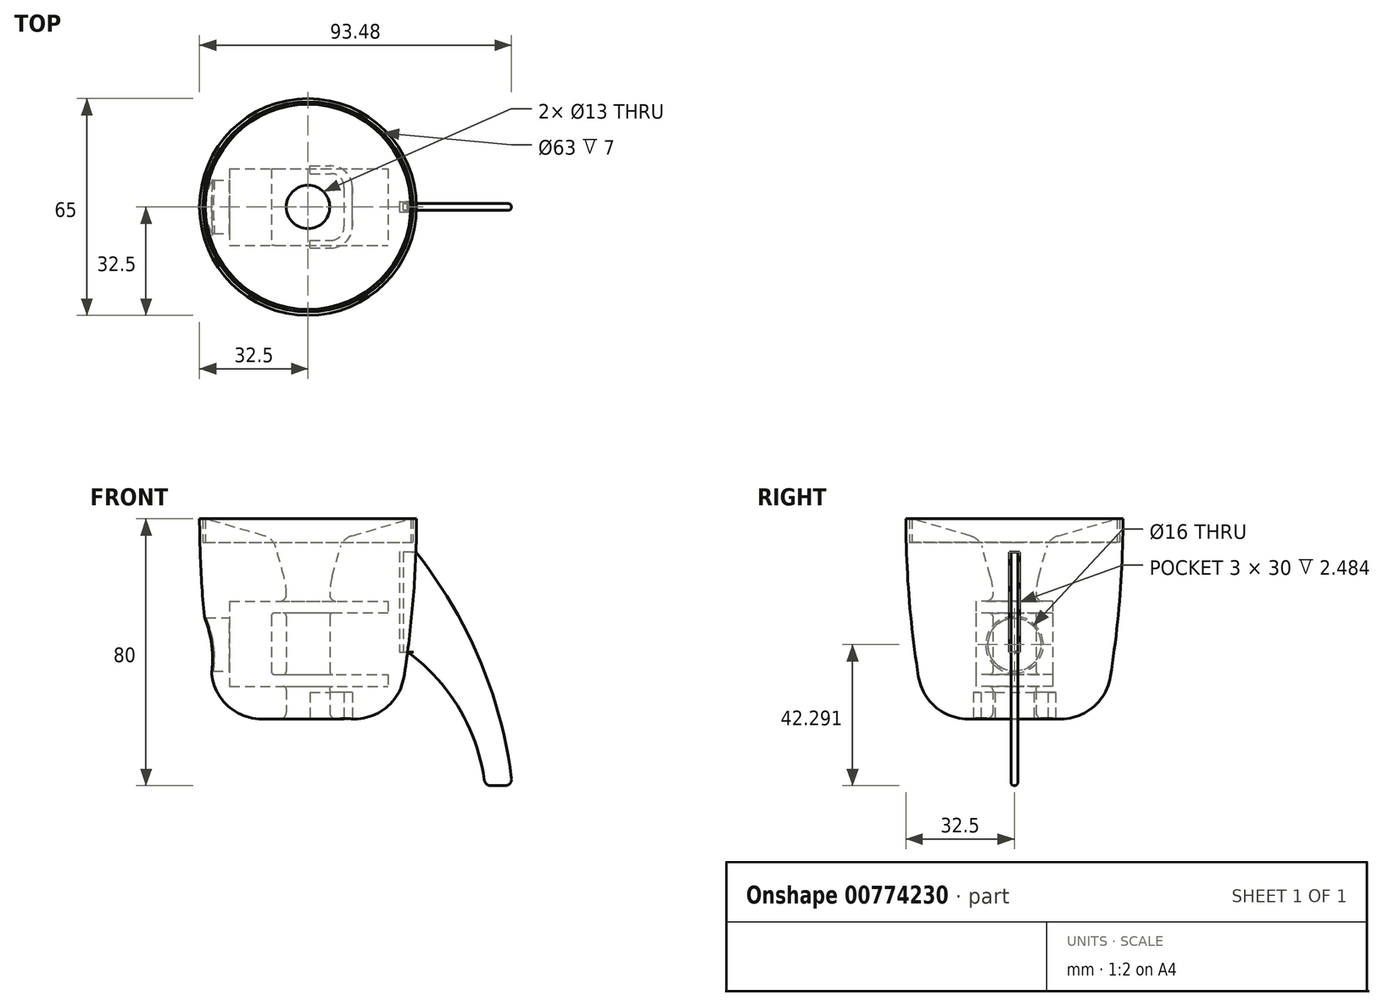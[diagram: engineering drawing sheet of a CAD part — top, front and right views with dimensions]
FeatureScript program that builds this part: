
annotation { "Feature Type Name" : "Feature", "Feature Type Description" : "" }
export const myFeature = defineFeature(function(context is Context, id is Id, definition is map)
    precondition{}
    {
        {
            var Q0;
            Q0=qCreatedBy(makeId("Front.planeOp"),FACE);
            var sketch = newSketch(context, id + "F0", { "sketchPlane" : qUnion([Q0])});
            skLineSegment(sketch, "E0", {"start": v(-32.5, -33.38) * mm, "end": v(-32.5, 26.62) * mm, "construction": true});
            skLineSegment(sketch, "E1", {"start": v(-30.75, 26.62) * mm, "end": v(-13.09, 21.53) * mm});
            skLineSegment(sketch, "E2", {"start": v(-9.65, 18.05) * mm, "end": v(-7.22, 9.22) * mm});
            skLineSegment(sketch, "E3", {"start": v(-6.5, 3.91) * mm, "end": v(-6.5, -33.38) * mm});
            skLineSegment(sketch, "E4", {"start": v(-6.5, -33.38) * mm, "end": v(-32.5, -33.38) * mm, "construction": true});
            skLineSegment(sketch, "E5", {"start": v(0, -36.56) * mm, "end": v(0, 42.73) * mm, "construction": true});
            skArc(sketch, "E6", {"start": v(-32.5, 26.62) * mm, "mid": v(-31.56, 2.88) * mm, "end": v(-28.74, -20.7) * mm});
            skLineSegment(sketch, "E7.bottom", {"start": v(-25.31, 12.07) * mm, "end": v(8.69, 12.07) * mm, "construction": true});
            skLineSegment(sketch, "E7.top", {"start": v(-25.31, -7.93) * mm, "end": v(8.69, -7.93) * mm, "construction": true});
            skLineSegment(sketch, "E7.left", {"start": v(-25.31, 12.07) * mm, "end": v(-25.31, -7.93) * mm, "construction": true});
            skLineSegment(sketch, "E7.right", {"start": v(8.69, 12.07) * mm, "end": v(8.69, -7.93) * mm, "construction": true});
            skLineSegment(sketch, "E8", {"start": v(-32.5, 26.62) * mm, "end": v(-31.5, 26.62) * mm});
            skLineSegment(sketch, "E9", {"start": v(-31.5, 26.62) * mm, "end": v(-31.5, 19.62) * mm});
            skLineSegment(sketch, "E10", {"start": v(-31.5, 19.62) * mm, "end": v(-30.75, 19.62) * mm});
            skLineSegment(sketch, "E11", {"start": v(-30.75, 19.62) * mm, "end": v(-30.75, 26.62) * mm});
            skLineSegment(sketch, "E12", {"start": v(-6.5, -33.38) * mm, "end": v(-6.5, -33.38) * mm});
            skLineSegment(sketch, "E13", {"start": v(-6.5, -33.38) * mm, "end": v(-13.88, -33.38) * mm});
            skPoint(sketch, "E14.visualSharp", {"position": v(-10.4, 20.75) * mm});
            skArc(sketch, "E14.filletArc", {"start": v(-9.65, 18.05) * mm, "mid": v(-10.92, 20.24) * mm, "end": v(-13.09, 21.53) * mm});
            skPoint(sketch, "E15.visualSharp", {"position": v(-6.5, 6.62) * mm});
            skArc(sketch, "E15.filletArc", {"start": v(-6.5, 3.91) * mm, "mid": v(-6.68, 6.6) * mm, "end": v(-7.22, 9.22) * mm});
            skArc(sketch, "E16", {"start": v(-28.74, -20.7) * mm, "mid": v(-23.65, -29.78) * mm, "end": v(-13.88, -33.38) * mm});
            skSolve(sketch);
        }
        {
            var Q0;
            Q0 = qSketchRegion(id + "F0", true);
            var Q1;
            Q1=sQuery(id+"F0.wireOp",EDGE,"E5");
            revolve(context, id + "F1", {"surfaceOperationType" : NewSurfaceOperationType.NEW, "entities" : qUnion([Q0]), "axis" : qUnion([Q1]), "revolveType" : RevolveType.FULL});
        }
        {
            var Q0;
            Q0=qCreatedBy(makeId("Front.planeOp"),FACE);
            var sketch = newSketch(context, id + "F2", { "sketchPlane" : qUnion([Q0])});
            skLineSegment(sketch, "E17.bottom", {"start": v(-23.5, 1.91) * mm, "end": v(24, 1.91) * mm});
            skLineSegment(sketch, "E17.top", {"start": v(-23.5, -23.59) * mm, "end": v(24, -23.59) * mm});
            skLineSegment(sketch, "E17.left", {"start": v(-23.5, 1.91) * mm, "end": v(-23.5, -23.59) * mm});
            skLineSegment(sketch, "E17.right", {"start": v(24, 1.91) * mm, "end": v(24, -23.59) * mm, "construction": true});
            skLineSegment(sketch, "E18", {"start": v(24, 1.91) * mm, "end": v(24, -1.59) * mm});
            skLineSegment(sketch, "E19", {"start": v(24, -1.59) * mm, "end": v(-11, -1.59) * mm});
            skLineSegment(sketch, "E20", {"start": v(-11, -1.59) * mm, "end": v(-11, -20.09) * mm});
            skLineSegment(sketch, "E21", {"start": v(-11, -20.09) * mm, "end": v(24, -20.09) * mm});
            skLineSegment(sketch, "E22", {"start": v(24, -20.09) * mm, "end": v(24, -23.59) * mm});
            skSolve(sketch);
        }
        {
            var Q0;
            Q0 = qSketchRegion(id + "F2", true);
            extrude(context, id + "F3", {"entities" : qUnion([Q0]), "operationType" : NewBodyOperationType.REMOVE, "oppositeDirection" : true, "depth" : 23 * mm, "offsetDistance" : 25 * mm, "symmetric" : true});
        }
        {
            var Q0;
            Q0=qCreatedBy(makeId("Right.planeOp"),FACE);
            cPlane(context, id + "F4", {"entities" : qUnion([Q0]), "cplaneType" : CPlaneType.OFFSET, "offset" : 18 * mm, "oppositeDirection" : true, "width" : 150 * mm, "height" : 150 * mm});
        }
        {
            var Q0;
            Q0=qCreatedBy(id+"F4.planeOp",FACE);
            var sketch = newSketch(context, id + "F5", { "sketchPlane" : qUnion([Q0])});
            skCircle(sketch, "E23", {"center": v(0, -11.09) * mm, "radius": 8 * mm});
            skSolve(sketch);
        }
        {
            var Q0;
            Q0 = qSketchRegion(id + "F5", true);
            extrude(context, id + "F6", {"entities" : qUnion([Q0]), "operationType" : NewBodyOperationType.REMOVE, "oppositeDirection" : true, "depth" : 25 * mm, "offsetDistance" : 25 * mm});
        }
        {
            var Q0;
            Q0=makeQuery(id+"F6.boolean.opBoolean","INTERSECT",EDGE,{"derivedFrom":[makeQuery(id+"F1.opRevolve","SWEPT_FACE",FACE,{"disambiguationData":[OSD([sQuery(id+"F0.wireOp",EDGE,"E6")])]}),makeQuery(id+"F6.opExtrude","SWEPT_FACE",FACE,{"disambiguationData":[OSD([sQuery(id+"F5.wireOp",EDGE,"E23")])]})]});
            fillet(context, id + "F7", {"entities" : qUnion([Q0]), "radius" : 0.5 * mm, "tangentPropagation" : true, "allowEdgeOverflow" : false});
        }
        {
            var Q0;
            Q0=makeQuery(id+"F1.opRevolve","SWEPT_EDGE",EDGE,{"disambiguationData":[OSD([sQuery(id+"F0.wireOp",EDGE,"E12"),sQuery(id+"F0.wireOp",EDGE,"E13")])]});
            fillet(context, id + "F8", {"entities" : qUnion([Q0]), "radius" : 2 * mm, "tangentPropagation" : true, "allowEdgeOverflow" : false});
        }
        {
            var Q0;
            Q0=makeQuery(id+"F3.boolean.opBoolean","INTERSECT",EDGE,{"derivedFrom":[makeQuery(id+"F1.opRevolve","SWEPT_FACE",FACE,{"disambiguationData":[OSD([sQuery(id+"F0.wireOp",EDGE,"E3"),sQuery(id+"F0.wireOp",EDGE,"E12")])]}),makeQuery(id+"F3.opExtrude","SWEPT_FACE",FACE,{"disambiguationData":[OSD([sQuery(id+"F2.wireOp",EDGE,"E17.top")])]})]});
            var Q1;
            Q1=makeQuery(id+"F3.boolean.opBoolean","INTERSECT",EDGE,{"derivedFrom":[makeQuery(id+"F1.opRevolve","SWEPT_FACE",FACE,{"disambiguationData":[OSD([sQuery(id+"F0.wireOp",EDGE,"E3"),sQuery(id+"F0.wireOp",EDGE,"E12")])]}),makeQuery(id+"F3.opExtrude","SWEPT_FACE",FACE,{"disambiguationData":[OSD([sQuery(id+"F2.wireOp",EDGE,"E21")])]})]});
            var Q2;
            Q2=makeQuery(id+"F3.boolean.opBoolean","INTERSECT",EDGE,{"derivedFrom":[makeQuery(id+"F1.opRevolve","SWEPT_FACE",FACE,{"disambiguationData":[OSD([sQuery(id+"F0.wireOp",EDGE,"E3"),sQuery(id+"F0.wireOp",EDGE,"E12")])]}),makeQuery(id+"F3.opExtrude","SWEPT_FACE",FACE,{"disambiguationData":[OSD([sQuery(id+"F2.wireOp",EDGE,"E19")])]})]});
            var Q3;
            Q3=makeQuery(id+"F3.boolean.opBoolean","COPY",EDGE,{"derivedFrom":makeQuery(id+"F3.opExtrude","SWEPT_EDGE",EDGE,{"disambiguationData":[OSD([sQuery(id+"F2.wireOp",EDGE,"E19"),sQuery(id+"F2.wireOp",EDGE,"E20")])]})});
            var Q4;
            Q4=makeQuery(id+"F3.boolean.opBoolean","COPY",EDGE,{"derivedFrom":makeQuery(id+"F3.opExtrude","SWEPT_EDGE",EDGE,{"disambiguationData":[OSD([sQuery(id+"F2.wireOp",EDGE,"E20"),sQuery(id+"F2.wireOp",EDGE,"E21")])]})});
            fillet(context, id + "F9", {"entities" : qUnion([Q0, Q1, Q2, Q3, Q4]), "radius" : 1 * mm, "tangentPropagation" : true, "allowEdgeOverflow" : false});
        }
        {
            var Q0;
            Q0=qCreatedBy(makeId("Front.planeOp"),FACE);
            var sketch = newSketch(context, id + "F10", { "sketchPlane" : qUnion([Q0])});
            skLineSegment(sketch, "E24", {"start": v(0.05, 26.62) * mm, "end": v(33.55, 26.62) * mm, "construction": true});
            skLineSegment(sketch, "E25", {"start": v(0.05, 26.62) * mm, "end": v(-32.5, 26.62) * mm, "construction": true});
            skArc(sketch, "E26", {"start": v(-32.5, 26.62) * mm, "mid": v(-31.56, 2.88) * mm, "end": v(-28.74, -20.7) * mm, "construction": true});
            skArc(sketch, "E27.MirrorCS", {"start": v(32.5, 26.62) * mm, "mid": v(31.56, 2.88) * mm, "end": v(28.74, -20.7) * mm, "construction": true});
            skArc(sketch, "E28", {"start": v(29.82, -13.38) * mm, "mid": v(31.45, 1.58) * mm, "end": v(32.33, 16.62) * mm});
            skLineSegment(sketch, "E29", {"start": v(32.33, 16.62) * mm, "end": v(27.33, 16.62) * mm});
            skLineSegment(sketch, "E30", {"start": v(27.33, 16.62) * mm, "end": v(27.33, -13.38) * mm});
            skLineSegment(sketch, "E31", {"start": v(27.33, -13.38) * mm, "end": v(29.82, -13.38) * mm});
            skLineSegment(sketch, "E32", {"start": v(0.05, 26.62) * mm, "end": v(0, 0) * mm, "construction": true});
            skSolve(sketch);
        }
        {
            var Q0;
            Q0 = qSketchRegion(id + "F10", true);
            extrude(context, id + "F11", {"entities" : qUnion([Q0]), "operationType" : NewBodyOperationType.REMOVE, "oppositeDirection" : true, "depth" : 3 * mm, "offsetDistance" : 25 * mm, "symmetric" : true});
        }
        {
            var Q0;
            Q0=qCreatedBy(makeId("Front.planeOp"),FACE);
            var sketch = newSketch(context, id + "F12", { "sketchPlane" : qUnion([Q0])});
            skLineSegment(sketch, "E33", {"start": v(32.32, 16.62) * mm, "end": v(28.5, 16.62) * mm});
            skLineSegment(sketch, "E34", {"start": v(28.5, 16.62) * mm, "end": v(28.5, -13.38) * mm});
            skLineSegment(sketch, "E35", {"start": v(28.5, -13.38) * mm, "end": v(29.94, -13.38) * mm});
            skLineSegment(sketch, "E36", {"start": v(54.8, -53.38) * mm, "end": v(58.98, -53.38) * mm});
            skArc(sketch, "E37", {"start": v(60.97, -51.13) * mm, "mid": v(51.29, -15.3) * mm, "end": v(32.32, 16.62) * mm});
            skArc(sketch, "E38", {"start": v(52.82, -51.66) * mm, "mid": v(45.26, -30.2) * mm, "end": v(29.94, -13.38) * mm});
            skPoint(sketch, "E39.visualSharp", {"position": v(53.03, -53.38) * mm});
            skArc(sketch, "E39.filletArc", {"start": v(52.82, -51.66) * mm, "mid": v(53.48, -52.9) * mm, "end": v(54.8, -53.38) * mm});
            skPoint(sketch, "E40.visualSharp", {"position": v(61.24, -53.38) * mm});
            skArc(sketch, "E40.filletArc", {"start": v(58.98, -53.38) * mm, "mid": v(60.48, -52.7) * mm, "end": v(60.97, -51.13) * mm});
            skSolve(sketch);
        }
        {
            var Q0;
            Q0 = qSketchRegion(id + "F12", true);
            extrude(context, id + "F13", {"entities" : qUnion([Q0]), "depth" : 2 * mm, "offsetDistance" : 25 * mm, "symmetric" : true});
        }
        {
            var Q0;
            Q0=makeQuery(id+"F13.opExtrude","CAP_EDGE",EDGE,{"disambiguationData":[OSD([sQuery(id+"F12.wireOp",EDGE,"E37")])],"isStart":false});
            var Q1;
            Q1=makeQuery(id+"F13.opExtrude","CAP_EDGE",EDGE,{"disambiguationData":[OSD([sQuery(id+"F12.wireOp",EDGE,"E37")])],"isStart":true});
            fillet(context, id + "F14", {"entities" : qUnion([Q0, Q1]), "radius" : 1 * mm, "tangentPropagation" : true, "allowEdgeOverflow" : false});
        }
        {
            var Q0;
            Q0=qCreatedBy(makeId("Top.planeOp"),FACE);
            cPlane(context, id + "F15", {"entities" : qUnion([Q0]), "cplaneType" : CPlaneType.OFFSET, "offset" : 2 * mm, "width" : 150 * mm, "height" : 150 * mm});
        }
        {
            var Q0;
            Q0=makeQuery(id+"F1.opRevolve","SWEPT_FACE",FACE,{"disambiguationData":[OSD([sQuery(id+"F0.wireOp",EDGE,"E13")])]});
            var sketch = newSketch(context, id + "F16", { "sketchPlane" : qUnion([Q0])});
            skLineSegment(sketch, "E41", {"start": v(0.57, 12.3) * mm, "end": v(0.57, 10) * mm});
            skLineSegment(sketch, "E42", {"start": v(0.57, 10) * mm, "end": v(6.85, 10) * mm});
            skLineSegment(sketch, "E43", {"start": v(0.57, -10) * mm, "end": v(6.85, -10) * mm});
            skLineSegment(sketch, "E44", {"start": v(0.57, -10) * mm, "end": v(0.57, -12.3) * mm});
            skLineSegment(sketch, "E45", {"start": v(0.57, -12.3) * mm, "end": v(6.85, -12.3) * mm});
            skLineSegment(sketch, "E46", {"start": v(10.78, -5.86) * mm, "end": v(10.78, 5.86) * mm});
            skLineSegment(sketch, "E47", {"start": v(13.28, 5.86) * mm, "end": v(13.28, -5.86) * mm});
            skLineSegment(sketch, "E48", {"start": v(0.57, 12.3) * mm, "end": v(6.85, 12.3) * mm});
            skArc(sketch, "E49", {"start": v(10.78, 5.86) * mm, "mid": v(9.7, 8.78) * mm, "end": v(6.85, 10) * mm});
            skArc(sketch, "E50", {"start": v(13.28, 5.86) * mm, "mid": v(11.4, 10.42) * mm, "end": v(6.85, 12.3) * mm});
            skArc(sketch, "E51", {"start": v(6.85, -10) * mm, "mid": v(9.7, -8.78) * mm, "end": v(10.78, -5.86) * mm});
            skArc(sketch, "E52", {"start": v(6.85, -12.3) * mm, "mid": v(11.4, -10.42) * mm, "end": v(13.28, -5.86) * mm});
            skSolve(sketch);
        }
        {
            var Q0;
            Q0 = qSketchRegion(id + "F16", true);
            var Q1;
            Q1=sQuery(id+"F16.wireOp",EDGE,"E49");
            var Q2;
            Q2=sQuery(id+"F16.wireOp",EDGE,"E50");
            var Q3;
            Q3=sQuery(id+"F16.wireOp",EDGE,"E51");
            var Q4;
            Q4=sQuery(id+"F16.wireOp",EDGE,"E52");
            var Q5;
            Q5=sQuery(id+"F16.wireOp",EDGE,"E42");
            var Q6;
            Q6=sQuery(id+"F16.wireOp",EDGE,"E43");
            var Q7;
            Q7=sQuery(id+"F16.wireOp",EDGE,"E45");
            var Q8;
            Q8=sQuery(id+"F16.wireOp",EDGE,"E46");
            var Q9;
            Q9=sQuery(id+"F16.wireOp",EDGE,"E47");
            var Q10;
            Q10=sQuery(id+"F16.wireOp",EDGE,"E48");
            var Q11;
            Q11=sQuery(id+"F16.wireOp",EDGE,"E41");
            var Q12;
            Q12=sQuery(id+"F16.wireOp",EDGE,"E44");
            extrude(context, id + "F17", {"entities" : qUnion([Q0]), "operationType" : NewBodyOperationType.REMOVE, "surfaceEntities" : qUnion([Q1, Q2, Q3, Q4, Q5, Q6, Q7, Q8, Q9, Q10, Q11, Q12]), "oppositeDirection" : true, "depth" : 8 * mm, "offsetDistance" : 25 * mm});
        }
        {
            var Q0;
            Q0=qCreatedBy(makeId("Top.planeOp"),FACE);
            var Q1;
            Q1=makeQuery(id+"F3.boolean.opBoolean","COPY",VERTEX,{"derivedFrom":makeQuery(id+"F3.opExtrude","CAP_VERTEX",VERTEX,{"disambiguationData":[OSD([sQuery(id+"F2.wireOp",EDGE,"E17.bottom"),sQuery(id+"F2.wireOp",EDGE,"E17.left")])],"isStart":true})});
            cPlane(context, id + "F18", {"entities" : qUnion([Q0, Q1]), "cplaneType" : CPlaneType.PLANE_POINT, "offset" : 25 * mm, "width" : 150 * mm, "height" : 150 * mm});
        }
        {
            var Q0;
            Q0=makeQuery(id+"F3.boolean.opBoolean","INTERSECT",EDGE,{"derivedFrom":[makeQuery(id+"F1.opRevolve","SWEPT_FACE",FACE,{"disambiguationData":[OSD([sQuery(id+"F0.wireOp",EDGE,"E3")])]}),makeQuery(id+"F3.opExtrude","SWEPT_FACE",FACE,{"disambiguationData":[OSD([sQuery(id+"F2.wireOp",EDGE,"E17.bottom")])]})]});
            fillet(context, id + "F19", {"entities" : qUnion([Q0]), "radius" : 2 * mm, "tangentPropagation" : true, "allowEdgeOverflow" : false});
        }
    });
